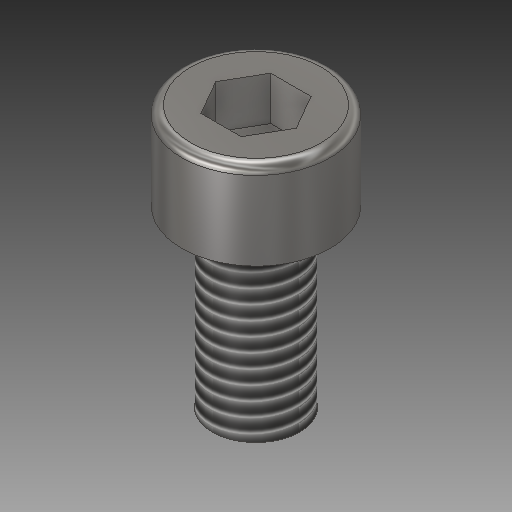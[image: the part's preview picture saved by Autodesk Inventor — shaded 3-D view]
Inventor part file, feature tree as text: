
AUTODESK INVENTOR PART (.ipt)
format: ipt  version: 2019 (Build 230136000, 136)  size: 175,104 bytes
history: native  units: mm
features: other x3, extrude x2, fillet x1
ambient origin geometry x8: Origin, YZ Plane, XZ Plane, XY Plane, X Axis, Y Axis, Z Axis, Center Point
bodies: Solid1 (feature_tree), Body (feature_tree)
feature tree (6):
  extrude  "Cap"  Depth=8.5mm
  extrude  "Key Socket Cutout"  Depth=5.0mm TaperAngle=0.0deg
  fillet  "Cap Fillet"  Radius=4.0mm
  other  "Cap Cross Section"
  other  "Key Socket Cutout Outline"
  other  "Body Cross Section"
